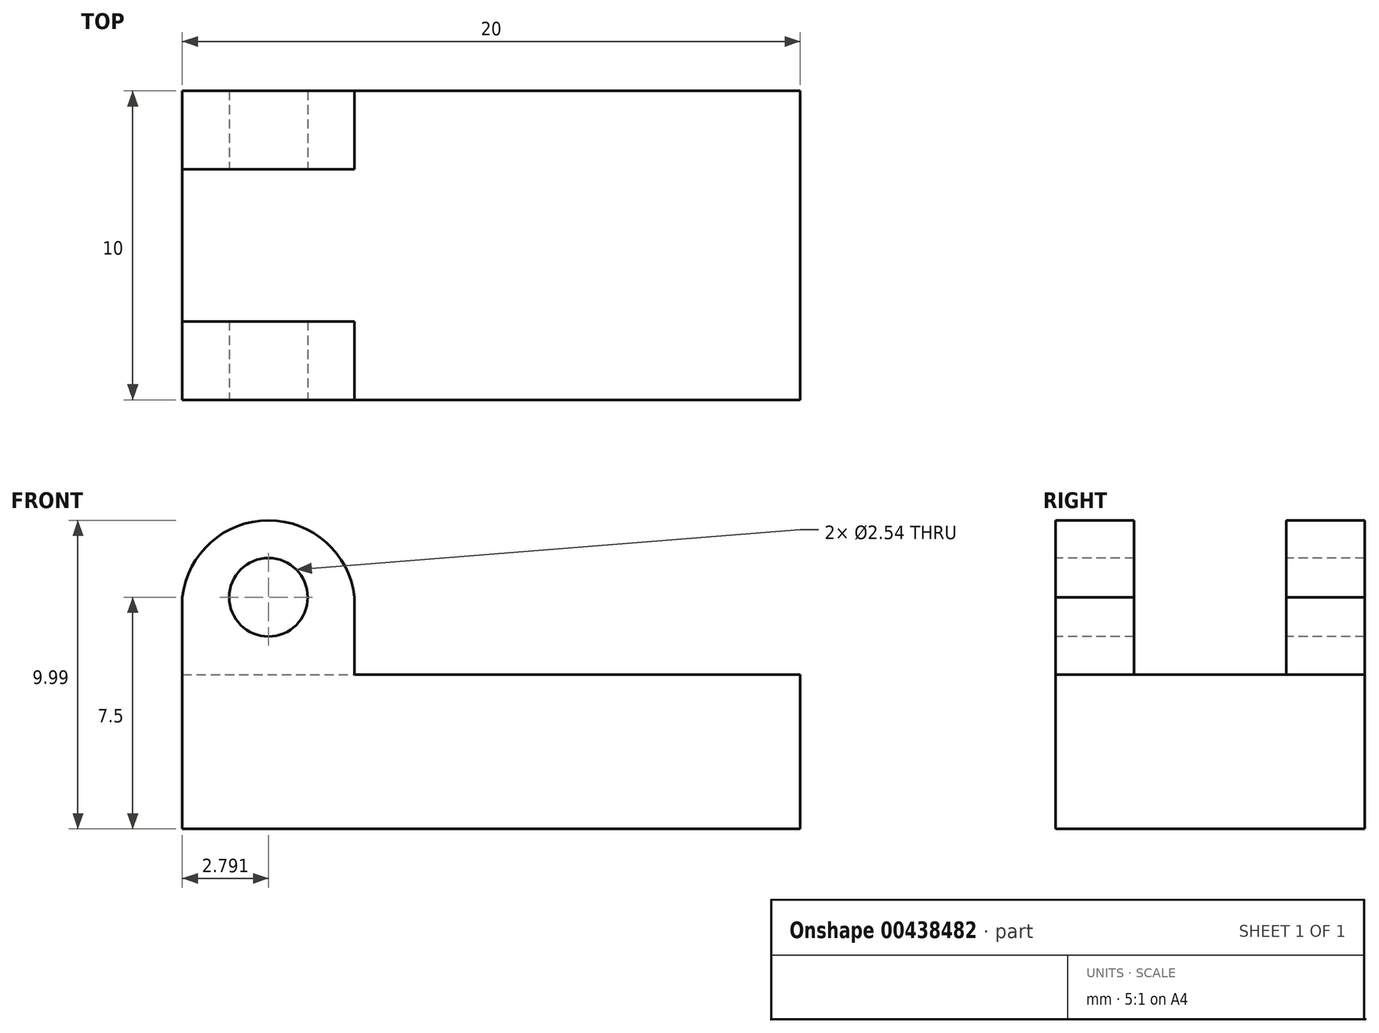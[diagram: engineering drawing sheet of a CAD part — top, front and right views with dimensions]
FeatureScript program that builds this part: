
annotation { "Feature Type Name" : "Feature", "Feature Type Description" : "" }
export const myFeature = defineFeature(function(context is Context, id is Id, definition is map)
    precondition{}
    {
        {
            var Q0;
            Q0=qCreatedBy(makeId("Top.planeOp"),FACE);
            var sketch = newSketch(context, id + "F0", { "sketchPlane" : qUnion([Q0])});
            skLineSegment(sketch, "E0.bottom", {"start": v(-8.65, -1.87) * mm, "end": v(11.35, -1.87) * mm});
            skLineSegment(sketch, "E0.top", {"start": v(-8.65, -11.87) * mm, "end": v(11.35, -11.87) * mm});
            skLineSegment(sketch, "E0.left", {"start": v(-8.65, -1.87) * mm, "end": v(-8.65, -11.87) * mm});
            skLineSegment(sketch, "E0.right", {"start": v(11.35, -1.87) * mm, "end": v(11.35, -11.87) * mm});
            skSolve(sketch);
        }
        {
            var Q0;
            Q0=makeQuery(id+"F0.imprint","IMPRINT",FACE,{"disambiguationData":[TD([[makeQuery(id+"F0.imprint","IMPRINT",EDGE,{"derivedFrom":sQuery(id+"F0.wireOp",EDGE,"E0.bottom")}),-1.0]])]});
            extrude(context, id + "F1", {"entities" : qUnion([Q0]), "depth" : 5 * mm});
        }
        {
            var Q0;
            Q0=makeQuery(id+"F1.opExtrude","CAP_FACE",FACE,{"disambiguationData":[OSD([sQuery(id+"F0.wireOp",EDGE,"E0.bottom"),sQuery(id+"F0.wireOp",EDGE,"E0.top"),sQuery(id+"F0.wireOp",EDGE,"E0.left"),sQuery(id+"F0.wireOp",EDGE,"E0.right")])],"isStart":false});
            var sketch = newSketch(context, id + "F2", { "sketchPlane" : qUnion([Q0])});
            skLineSegment(sketch, "E1.bottom", {"start": v(-8.65, -1.87) * mm, "end": v(-3.07, -1.87) * mm});
            skLineSegment(sketch, "E1.top", {"start": v(-8.65, -4.4) * mm, "end": v(-3.07, -4.4) * mm});
            skLineSegment(sketch, "E1.left", {"start": v(-8.65, -1.87) * mm, "end": v(-8.65, -4.4) * mm});
            skLineSegment(sketch, "E1.right", {"start": v(-3.07, -1.87) * mm, "end": v(-3.07, -4.4) * mm});
            skLineSegment(sketch, "E2", {"start": v(-8.65, -6.87) * mm, "end": v(11.35, -6.87) * mm, "construction": true});
            skLineSegment(sketch, "E3.MirrorCS", {"start": v(-8.65, -9.33) * mm, "end": v(-3.07, -9.33) * mm});
            skLineSegment(sketch, "E4.MirrorCS", {"start": v(-3.07, -11.87) * mm, "end": v(-3.07, -9.33) * mm});
            skLineSegment(sketch, "E5.MirrorCS", {"start": v(-8.65, -11.87) * mm, "end": v(-8.65, -9.33) * mm});
            skLineSegment(sketch, "E6.MirrorCS", {"start": v(-8.65, -11.87) * mm, "end": v(-3.07, -11.87) * mm});
            skSolve(sketch);
        }
        {
            var Q0;
            Q0=makeQuery(id+"F2.imprint","IMPRINT",FACE,{"disambiguationData":[TD([[makeQuery(id+"F2.imprint","IMPRINT",EDGE,{"derivedFrom":sQuery(id+"F2.wireOp",EDGE,"E1.bottom")}),-1.0]])]});
            var Q1;
            Q1=makeQuery(id+"F2.imprint","IMPRINT",FACE,{"disambiguationData":[TD([[makeQuery(id+"F2.imprint","IMPRINT",EDGE,{"derivedFrom":sQuery(id+"F2.wireOp",EDGE,"E3.MirrorCS")}),-1.0]])]});
            extrude(context, id + "F3", {"entities" : qUnion([Q0, Q1]), "operationType" : NewBodyOperationType.ADD, "depth" : 5 * mm});
        }
        {
            var Q0;
            Q0=makeQuery(id+"F3.boolean.opBoolean","MERGE",FACE,{"derivedFrom":[makeQuery(id+"F1.opExtrude","SWEPT_FACE",FACE,{"disambiguationData":[OSD([sQuery(id+"F0.wireOp",EDGE,"E0.top")])]}),makeQuery(id+"F3.opExtrude","SWEPT_FACE",FACE,{"disambiguationData":[OSD([sQuery(id+"F2.wireOp",EDGE,"E6.MirrorCS")])]})]});
            var sketch = newSketch(context, id + "F4", { "sketchPlane" : qUnion([Q0])});
            skArc(sketch, "E7", {"start": v(-3.07, 7.5) * mm, "mid": v(-5.86, 9.99) * mm, "end": v(-8.65, 7.5) * mm});
            skPoint(sketch, "E7.endSnap0", {"position": v(-3.07, 7.5) * mm});
            skLineSegment(sketch, "E8", {"start": v(-8.65, 7.5) * mm, "end": v(-9.73, 7.92) * mm});
            skLineSegment(sketch, "E9", {"start": v(-9.73, 7.92) * mm, "end": v(-9.26, 10.9) * mm});
            skLineSegment(sketch, "E10", {"start": v(-9.26, 10.9) * mm, "end": v(-2.42, 10.9) * mm});
            skLineSegment(sketch, "E11", {"start": v(-2.42, 10.9) * mm, "end": v(-2.42, 7.5) * mm});
            skLineSegment(sketch, "E12", {"start": v(-2.42, 7.5) * mm, "end": v(-3.07, 7.5) * mm});
            skSolve(sketch);
        }
        {
            var Q0;
            {var subQ4=sQuery(id+"F4.wireOp",EDGE,"E8");Q0=makeQuery(id+"F4.imprint","IMPRINT",FACE,{"disambiguationData":[TD([[makeQuery(id+"F4.imprint","IMPRINT",EDGE,{"derivedFrom":subQ4}),-1.0]])]});}
            var Q1;
            {var subQ0=sQuery(id+"F4.wireOp",EDGE,"E7");Q1=makeQuery(id+"F4.imprint","IMPRINT",FACE,{"disambiguationData":[TD([[makeQuery(id+"F4.imprint","IMPRINT",EDGE,{"derivedFrom":subQ0}),-1.0]])]});}
            extrude(context, id + "F5", {"entities" : qUnion([Q0, Q1]), "operationType" : NewBodyOperationType.REMOVE, "endBound" : BoundingType.THROUGH_ALL, "oppositeDirection" : true, "depth" : 25.4 * mm});
        }
        {
            var Q0;
            Q0=makeQuery(id+"F3.boolean.opBoolean","MERGE",FACE,{"derivedFrom":[makeQuery(id+"F1.opExtrude","SWEPT_FACE",FACE,{"disambiguationData":[OSD([sQuery(id+"F0.wireOp",EDGE,"E0.top")])]}),makeQuery(id+"F3.opExtrude","SWEPT_FACE",FACE,{"disambiguationData":[OSD([sQuery(id+"F2.wireOp",EDGE,"E6.MirrorCS")])]})]});
            var sketch = newSketch(context, id + "F6", { "sketchPlane" : qUnion([Q0])});
            skLineSegment(sketch, "E13", {"start": v(-8.65, 7.5) * mm, "end": v(-3.07, 7.5) * mm, "construction": true});
            skLineSegment(sketch, "E14", {"start": v(-5.86, 7.5) * mm, "end": v(-5.86, 9.99) * mm, "construction": true});
            skCircle(sketch, "E15", {"center": v(-5.86, 7.5) * mm, "radius": 1.27 * mm});
            skSolve(sketch);
        }
        {
            var Q0;
            Q0 = qSketchRegion(id + "F6", true);
            extrude(context, id + "F7", {"entities" : qUnion([Q0]), "operationType" : NewBodyOperationType.REMOVE, "endBound" : BoundingType.THROUGH_ALL, "oppositeDirection" : true, "depth" : 25.4 * mm});
        }
    });
